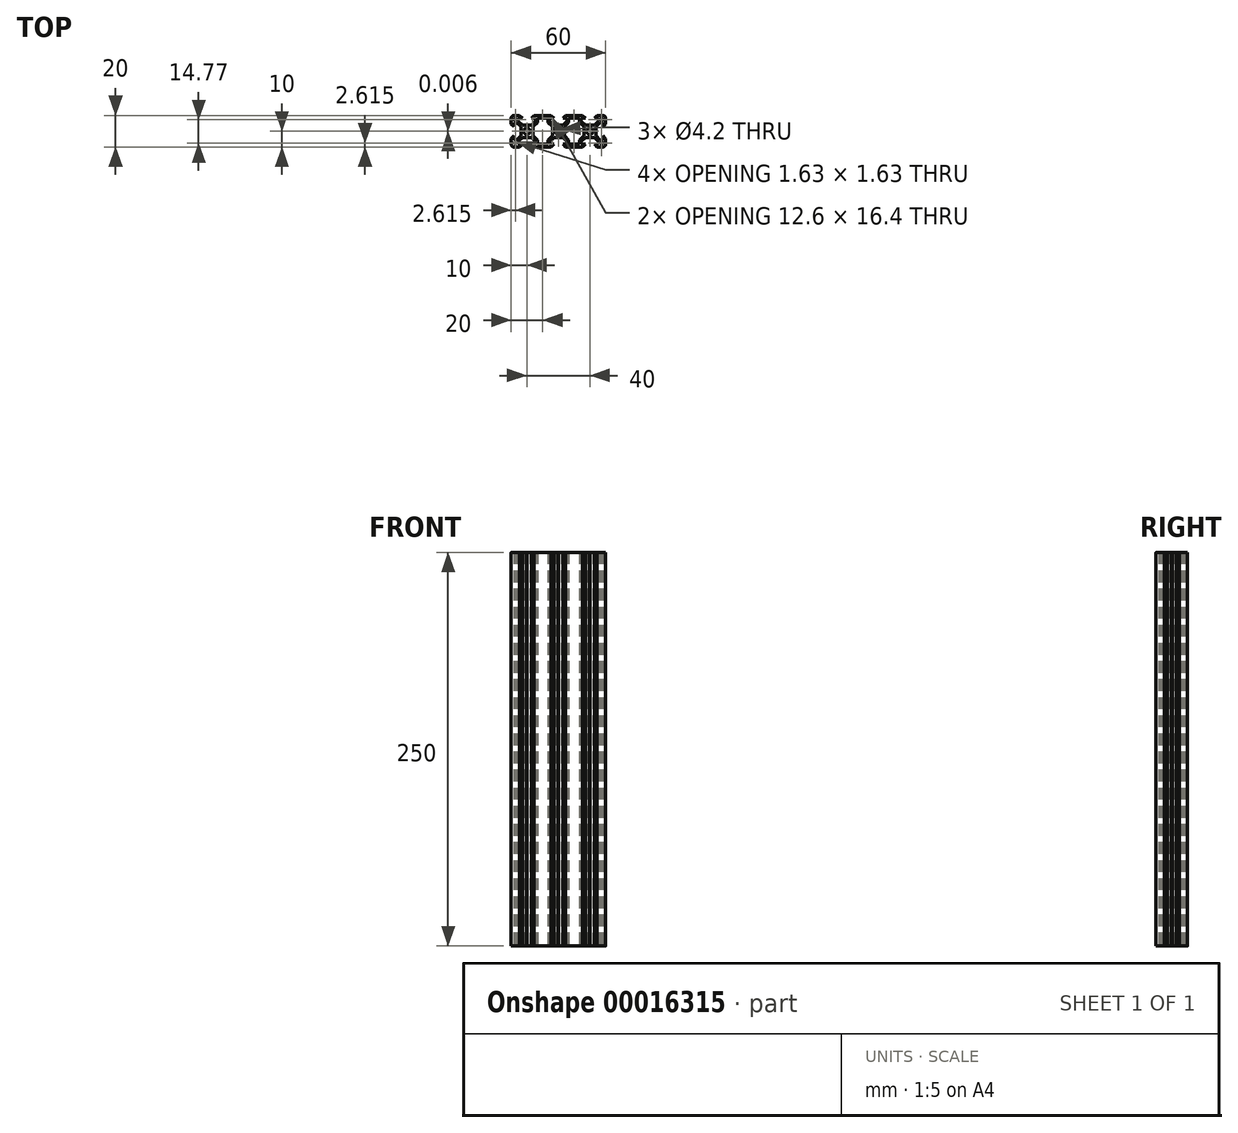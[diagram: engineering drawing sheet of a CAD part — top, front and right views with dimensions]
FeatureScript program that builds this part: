
annotation { "Feature Type Name" : "Feature", "Feature Type Description" : "" }
export const myFeature = defineFeature(function(context is Context, id is Id, definition is map)
    precondition{}
    {
        {
            var Q0;
            Q0=qCreatedBy(makeId("Top.planeOp"),FACE);
            var sketch = newSketch(context, id + "F0", { "sketchPlane" : qUnion([Q0])});
            skCircle(sketch, "E0", {"center": v(20, 0) * mm, "radius": 2.1 * mm});
            skLineSegment(sketch, "E1", {"start": v(-16.1, -2.84) * mm, "end": v(-13.43, -5.5) * mm});
            skLineSegment(sketch, "E2", {"start": v(-16.1, -0.2) * mm, "end": v(-16.1, -2.84) * mm});
            skLineSegment(sketch, "E3", {"start": v(-16.3, 0) * mm, "end": v(-16.1, -0.2) * mm});
            skLineSegment(sketch, "E4", {"start": v(-16.1, 0.2) * mm, "end": v(-16.3, 0) * mm});
            skLineSegment(sketch, "E5", {"start": v(-16.1, 2.84) * mm, "end": v(-16.1, 0.2) * mm});
            skLineSegment(sketch, "E6", {"start": v(-13.43, 5.5) * mm, "end": v(-16.1, 2.84) * mm});
            skLineSegment(sketch, "E7", {"start": v(-13.43, 8.2) * mm, "end": v(-13.43, 5.5) * mm});
            skLineSegment(sketch, "E8", {"start": v(-6.57, 8.2) * mm, "end": v(-13.43, 8.2) * mm});
            skLineSegment(sketch, "E9", {"start": v(-6.57, 5.5) * mm, "end": v(-6.57, 8.2) * mm});
            skLineSegment(sketch, "E10", {"start": v(-3.9, 2.84) * mm, "end": v(-6.57, 5.5) * mm});
            skLineSegment(sketch, "E11", {"start": v(-3.9, 0.2) * mm, "end": v(-3.9, 2.84) * mm});
            skLineSegment(sketch, "E12", {"start": v(-3.7, 0) * mm, "end": v(-3.9, 0.2) * mm});
            skLineSegment(sketch, "E13", {"start": v(-3.9, -0.2) * mm, "end": v(-3.7, 0) * mm});
            skLineSegment(sketch, "E14", {"start": v(-3.9, -2.84) * mm, "end": v(-3.9, -0.2) * mm});
            skLineSegment(sketch, "E15", {"start": v(-6.57, -5.5) * mm, "end": v(-3.9, -2.84) * mm});
            skLineSegment(sketch, "E16", {"start": v(-6.57, -8.2) * mm, "end": v(-6.57, -5.5) * mm});
            skLineSegment(sketch, "E17", {"start": v(-13.43, -8.2) * mm, "end": v(-6.57, -8.2) * mm});
            skLineSegment(sketch, "E18", {"start": v(-13.43, -5.5) * mm, "end": v(-13.43, -8.2) * mm});
            skLineSegment(sketch, "E19", {"start": v(26.57, 7.66) * mm, "end": v(27.66, 6.57) * mm});
            skLineSegment(sketch, "E20", {"start": v(26.57, 8.2) * mm, "end": v(26.57, 7.66) * mm});
            skLineSegment(sketch, "E21", {"start": v(28.2, 8.2) * mm, "end": v(26.57, 8.2) * mm});
            skLineSegment(sketch, "E22", {"start": v(28.2, 6.57) * mm, "end": v(28.2, 8.2) * mm});
            skLineSegment(sketch, "E23", {"start": v(27.66, 6.57) * mm, "end": v(28.2, 6.57) * mm});
            skLineSegment(sketch, "E24", {"start": v(27.66, -6.57) * mm, "end": v(26.57, -7.66) * mm});
            skLineSegment(sketch, "E25", {"start": v(28.2, -6.57) * mm, "end": v(27.66, -6.57) * mm});
            skLineSegment(sketch, "E26", {"start": v(28.2, -8.2) * mm, "end": v(28.2, -6.57) * mm});
            skLineSegment(sketch, "E27", {"start": v(26.57, -8.2) * mm, "end": v(28.2, -8.2) * mm});
            skLineSegment(sketch, "E28", {"start": v(26.57, -7.66) * mm, "end": v(26.57, -8.2) * mm});
            skLineSegment(sketch, "E29", {"start": v(-26.57, -7.66) * mm, "end": v(-27.66, -6.57) * mm});
            skLineSegment(sketch, "E30", {"start": v(-26.57, -8.2) * mm, "end": v(-26.57, -7.66) * mm});
            skLineSegment(sketch, "E31", {"start": v(-28.2, -8.2) * mm, "end": v(-26.57, -8.2) * mm});
            skLineSegment(sketch, "E32", {"start": v(-28.2, -6.57) * mm, "end": v(-28.2, -8.2) * mm});
            skLineSegment(sketch, "E33", {"start": v(-27.66, -6.57) * mm, "end": v(-28.2, -6.57) * mm});
            skLineSegment(sketch, "E34", {"start": v(-27.66, 6.57) * mm, "end": v(-26.57, 7.66) * mm});
            skLineSegment(sketch, "E35", {"start": v(-28.2, 6.57) * mm, "end": v(-27.66, 6.57) * mm});
            skLineSegment(sketch, "E36", {"start": v(-28.2, 8.2) * mm, "end": v(-28.2, 6.57) * mm});
            skLineSegment(sketch, "E37", {"start": v(-26.57, 8.2) * mm, "end": v(-28.2, 8.2) * mm});
            skLineSegment(sketch, "E38", {"start": v(-26.57, 7.66) * mm, "end": v(-26.57, 8.2) * mm});
            skLineSegment(sketch, "E39", {"start": v(-25.5, 8.2) * mm, "end": v(-22.84, 8.2) * mm});
            skLineSegment(sketch, "E40", {"start": v(-22.84, 8.2) * mm, "end": v(-24.64, 10) * mm});
            skLineSegment(sketch, "E41", {"start": v(-24.64, 10) * mm, "end": v(-28.2, 10) * mm});
            skArc(sketch, "E42", {"start": v(-28.2, 10) * mm, "mid": v(-29.47, 9.47) * mm, "end": v(-30, 8.2) * mm});
            skLineSegment(sketch, "E43", {"start": v(-30, 8.2) * mm, "end": v(-30, 4.64) * mm});
            skLineSegment(sketch, "E44", {"start": v(-30, 4.64) * mm, "end": v(-28.2, 2.84) * mm});
            skLineSegment(sketch, "E45", {"start": v(-28.2, 2.84) * mm, "end": v(-28.2, 5.5) * mm});
            skLineSegment(sketch, "E46", {"start": v(-28.2, 5.5) * mm, "end": v(-26.56, 5.5) * mm});
            skLineSegment(sketch, "E47", {"start": v(-26.56, 5.5) * mm, "end": v(-23.9, 2.84) * mm});
            skLineSegment(sketch, "E48", {"start": v(-23.9, 2.84) * mm, "end": v(-23.9, 0.2) * mm});
            skLineSegment(sketch, "E49", {"start": v(-23.9, 0.2) * mm, "end": v(-23.7, 0) * mm});
            skLineSegment(sketch, "E50", {"start": v(-23.7, 0) * mm, "end": v(-23.9, -0.2) * mm});
            skLineSegment(sketch, "E51", {"start": v(-23.9, -0.2) * mm, "end": v(-23.9, -2.84) * mm});
            skLineSegment(sketch, "E52", {"start": v(-23.9, -2.84) * mm, "end": v(-26.56, -5.5) * mm});
            skLineSegment(sketch, "E53", {"start": v(-26.56, -5.5) * mm, "end": v(-28.2, -5.5) * mm});
            skLineSegment(sketch, "E54", {"start": v(-28.2, -5.5) * mm, "end": v(-28.2, -2.84) * mm});
            skLineSegment(sketch, "E55", {"start": v(-28.2, -2.84) * mm, "end": v(-30, -4.64) * mm});
            skLineSegment(sketch, "E56", {"start": v(-30, -4.64) * mm, "end": v(-30, -8.2) * mm});
            skArc(sketch, "E57", {"start": v(-30, -8.2) * mm, "mid": v(-29.47, -9.47) * mm, "end": v(-28.2, -10) * mm});
            skLineSegment(sketch, "E58", {"start": v(-28.2, -10) * mm, "end": v(-24.64, -10) * mm});
            skLineSegment(sketch, "E59", {"start": v(-24.64, -10) * mm, "end": v(-22.84, -8.2) * mm});
            skLineSegment(sketch, "E60", {"start": v(-22.84, -8.2) * mm, "end": v(-25.5, -8.2) * mm});
            skLineSegment(sketch, "E61", {"start": v(-25.5, -8.2) * mm, "end": v(-25.5, -6.56) * mm});
            skLineSegment(sketch, "E62", {"start": v(-25.5, -6.56) * mm, "end": v(-22.84, -3.9) * mm});
            skLineSegment(sketch, "E63", {"start": v(-22.84, -3.9) * mm, "end": v(-20.2, -3.9) * mm});
            skLineSegment(sketch, "E64", {"start": v(-20.2, -3.9) * mm, "end": v(-20, -3.7) * mm});
            skLineSegment(sketch, "E65", {"start": v(-20, -3.7) * mm, "end": v(-19.8, -3.9) * mm});
            skLineSegment(sketch, "E66", {"start": v(-19.8, -3.9) * mm, "end": v(-17.16, -3.9) * mm});
            skLineSegment(sketch, "E67", {"start": v(-17.16, -3.9) * mm, "end": v(-14.5, -6.56) * mm});
            skLineSegment(sketch, "E68", {"start": v(-14.5, -6.56) * mm, "end": v(-14.5, -8.2) * mm});
            skLineSegment(sketch, "E69", {"start": v(-14.5, -8.2) * mm, "end": v(-17.16, -8.2) * mm});
            skLineSegment(sketch, "E70", {"start": v(-17.16, -8.2) * mm, "end": v(-15.36, -10) * mm});
            skLineSegment(sketch, "E71", {"start": v(-15.36, -10) * mm, "end": v(-4.64, -10) * mm});
            skLineSegment(sketch, "E72", {"start": v(-4.64, -10) * mm, "end": v(-2.84, -8.2) * mm});
            skLineSegment(sketch, "E73", {"start": v(-2.84, -8.2) * mm, "end": v(-5.5, -8.2) * mm});
            skLineSegment(sketch, "E74", {"start": v(-5.5, -8.2) * mm, "end": v(-5.5, -6.56) * mm});
            skLineSegment(sketch, "E75", {"start": v(-5.5, -6.56) * mm, "end": v(-2.84, -3.9) * mm});
            skLineSegment(sketch, "E76", {"start": v(-2.84, -3.9) * mm, "end": v(-0.2, -3.9) * mm});
            skLineSegment(sketch, "E77", {"start": v(-0.2, -3.9) * mm, "end": v(0, -3.7) * mm});
            skLineSegment(sketch, "E78", {"start": v(0, -3.7) * mm, "end": v(0.2, -3.9) * mm});
            skLineSegment(sketch, "E79", {"start": v(0.2, -3.9) * mm, "end": v(2.84, -3.9) * mm});
            skLineSegment(sketch, "E80", {"start": v(2.84, -3.9) * mm, "end": v(5.5, -6.56) * mm});
            skLineSegment(sketch, "E81", {"start": v(5.5, -6.56) * mm, "end": v(5.5, -8.2) * mm});
            skLineSegment(sketch, "E82", {"start": v(5.5, -8.2) * mm, "end": v(2.84, -8.2) * mm});
            skLineSegment(sketch, "E83", {"start": v(2.84, -8.2) * mm, "end": v(4.64, -10) * mm});
            skLineSegment(sketch, "E84", {"start": v(4.64, -10) * mm, "end": v(15.36, -10) * mm});
            skLineSegment(sketch, "E85", {"start": v(15.36, -10) * mm, "end": v(17.16, -8.2) * mm});
            skLineSegment(sketch, "E86", {"start": v(17.16, -8.2) * mm, "end": v(14.5, -8.2) * mm});
            skLineSegment(sketch, "E87", {"start": v(14.5, -8.2) * mm, "end": v(14.5, -6.56) * mm});
            skLineSegment(sketch, "E88", {"start": v(14.5, -6.56) * mm, "end": v(17.16, -3.9) * mm});
            skLineSegment(sketch, "E89", {"start": v(17.16, -3.9) * mm, "end": v(19.8, -3.9) * mm});
            skLineSegment(sketch, "E90", {"start": v(19.8, -3.9) * mm, "end": v(20, -3.7) * mm});
            skLineSegment(sketch, "E91", {"start": v(20, -3.7) * mm, "end": v(20.2, -3.9) * mm});
            skLineSegment(sketch, "E92", {"start": v(20.2, -3.9) * mm, "end": v(22.84, -3.9) * mm});
            skLineSegment(sketch, "E93", {"start": v(22.84, -3.9) * mm, "end": v(25.5, -6.56) * mm});
            skLineSegment(sketch, "E94", {"start": v(25.5, -6.56) * mm, "end": v(25.5, -8.2) * mm});
            skLineSegment(sketch, "E95", {"start": v(25.5, -8.2) * mm, "end": v(22.84, -8.2) * mm});
            skLineSegment(sketch, "E96", {"start": v(22.84, -8.2) * mm, "end": v(24.64, -10) * mm});
            skLineSegment(sketch, "E97", {"start": v(24.64, -10) * mm, "end": v(28.2, -10) * mm});
            skArc(sketch, "E98", {"start": v(28.2, -10) * mm, "mid": v(29.47, -9.47) * mm, "end": v(30, -8.2) * mm});
            skLineSegment(sketch, "E99", {"start": v(30, -8.2) * mm, "end": v(30, -4.64) * mm});
            skLineSegment(sketch, "E100", {"start": v(30, -4.64) * mm, "end": v(28.2, -2.84) * mm});
            skLineSegment(sketch, "E101", {"start": v(28.2, -2.84) * mm, "end": v(28.2, -5.5) * mm});
            skLineSegment(sketch, "E102", {"start": v(28.2, -5.5) * mm, "end": v(26.56, -5.5) * mm});
            skLineSegment(sketch, "E103", {"start": v(26.56, -5.5) * mm, "end": v(23.9, -2.84) * mm});
            skLineSegment(sketch, "E104", {"start": v(23.9, -2.84) * mm, "end": v(23.9, -0.2) * mm});
            skLineSegment(sketch, "E105", {"start": v(23.9, -0.2) * mm, "end": v(23.7, 0) * mm});
            skLineSegment(sketch, "E106", {"start": v(23.7, 0) * mm, "end": v(23.9, 0.2) * mm});
            skLineSegment(sketch, "E107", {"start": v(23.9, 0.2) * mm, "end": v(23.9, 2.84) * mm});
            skLineSegment(sketch, "E108", {"start": v(23.9, 2.84) * mm, "end": v(26.56, 5.5) * mm});
            skLineSegment(sketch, "E109", {"start": v(26.56, 5.5) * mm, "end": v(28.2, 5.5) * mm});
            skLineSegment(sketch, "E110", {"start": v(28.2, 5.5) * mm, "end": v(28.2, 2.84) * mm});
            skLineSegment(sketch, "E111", {"start": v(28.2, 2.84) * mm, "end": v(30, 4.64) * mm});
            skLineSegment(sketch, "E112", {"start": v(30, 4.64) * mm, "end": v(30, 8.2) * mm});
            skArc(sketch, "E113", {"start": v(30, 8.2) * mm, "mid": v(29.47, 9.47) * mm, "end": v(28.2, 10) * mm});
            skLineSegment(sketch, "E114", {"start": v(28.2, 10) * mm, "end": v(24.64, 10) * mm});
            skLineSegment(sketch, "E115", {"start": v(24.64, 10) * mm, "end": v(22.84, 8.2) * mm});
            skLineSegment(sketch, "E116", {"start": v(22.84, 8.2) * mm, "end": v(25.5, 8.2) * mm});
            skLineSegment(sketch, "E117", {"start": v(25.5, 8.2) * mm, "end": v(25.5, 6.56) * mm});
            skLineSegment(sketch, "E118", {"start": v(25.5, 6.56) * mm, "end": v(22.84, 3.9) * mm});
            skLineSegment(sketch, "E119", {"start": v(22.84, 3.9) * mm, "end": v(20.2, 3.9) * mm});
            skLineSegment(sketch, "E120", {"start": v(20.2, 3.9) * mm, "end": v(20, 3.7) * mm});
            skLineSegment(sketch, "E121", {"start": v(20, 3.7) * mm, "end": v(19.8, 3.9) * mm});
            skLineSegment(sketch, "E122", {"start": v(19.8, 3.9) * mm, "end": v(17.16, 3.9) * mm});
            skLineSegment(sketch, "E123", {"start": v(17.16, 3.9) * mm, "end": v(14.5, 6.56) * mm});
            skLineSegment(sketch, "E124", {"start": v(14.5, 6.56) * mm, "end": v(14.5, 8.2) * mm});
            skLineSegment(sketch, "E125", {"start": v(14.5, 8.2) * mm, "end": v(17.16, 8.2) * mm});
            skLineSegment(sketch, "E126", {"start": v(17.16, 8.2) * mm, "end": v(15.36, 10) * mm});
            skLineSegment(sketch, "E127", {"start": v(15.36, 10) * mm, "end": v(4.64, 10) * mm});
            skLineSegment(sketch, "E128", {"start": v(4.64, 10) * mm, "end": v(2.84, 8.2) * mm});
            skLineSegment(sketch, "E129", {"start": v(2.84, 8.2) * mm, "end": v(5.5, 8.2) * mm});
            skLineSegment(sketch, "E130", {"start": v(5.5, 8.2) * mm, "end": v(5.5, 6.56) * mm});
            skLineSegment(sketch, "E131", {"start": v(5.5, 6.56) * mm, "end": v(2.84, 3.9) * mm});
            skLineSegment(sketch, "E132", {"start": v(2.84, 3.9) * mm, "end": v(0.2, 3.9) * mm});
            skLineSegment(sketch, "E133", {"start": v(0.2, 3.9) * mm, "end": v(0, 3.7) * mm});
            skLineSegment(sketch, "E134", {"start": v(0, 3.7) * mm, "end": v(-0.2, 3.9) * mm});
            skLineSegment(sketch, "E135", {"start": v(-0.2, 3.9) * mm, "end": v(-2.84, 3.9) * mm});
            skLineSegment(sketch, "E136", {"start": v(-2.84, 3.9) * mm, "end": v(-5.5, 6.56) * mm});
            skLineSegment(sketch, "E137", {"start": v(-5.5, 6.56) * mm, "end": v(-5.5, 8.2) * mm});
            skLineSegment(sketch, "E138", {"start": v(-5.5, 8.2) * mm, "end": v(-2.84, 8.2) * mm});
            skLineSegment(sketch, "E139", {"start": v(-2.84, 8.2) * mm, "end": v(-4.64, 10) * mm});
            skLineSegment(sketch, "E140", {"start": v(-4.64, 10) * mm, "end": v(-15.36, 10) * mm});
            skLineSegment(sketch, "E141", {"start": v(-15.36, 10) * mm, "end": v(-17.16, 8.2) * mm});
            skLineSegment(sketch, "E142", {"start": v(-17.16, 8.2) * mm, "end": v(-14.5, 8.2) * mm});
            skLineSegment(sketch, "E143", {"start": v(-14.5, 8.2) * mm, "end": v(-14.5, 6.56) * mm});
            skLineSegment(sketch, "E144", {"start": v(-14.5, 6.56) * mm, "end": v(-17.16, 3.9) * mm});
            skLineSegment(sketch, "E145", {"start": v(-17.16, 3.9) * mm, "end": v(-19.8, 3.9) * mm});
            skLineSegment(sketch, "E146", {"start": v(-19.8, 3.9) * mm, "end": v(-20, 3.7) * mm});
            skLineSegment(sketch, "E147", {"start": v(-20, 3.7) * mm, "end": v(-20.2, 3.9) * mm});
            skLineSegment(sketch, "E148", {"start": v(-20.2, 3.9) * mm, "end": v(-22.84, 3.9) * mm});
            skLineSegment(sketch, "E149", {"start": v(-22.84, 3.9) * mm, "end": v(-25.5, 6.56) * mm});
            skLineSegment(sketch, "E150", {"start": v(-25.5, 6.56) * mm, "end": v(-25.5, 8.2) * mm});
            skCircle(sketch, "E151", {"center": v(-20, 0) * mm, "radius": 2.1 * mm});
            skLineSegment(sketch, "E152", {"start": v(16.1, 0.2) * mm, "end": v(16.1, 2.84) * mm});
            skLineSegment(sketch, "E153", {"start": v(16.3, 0) * mm, "end": v(16.1, 0.2) * mm});
            skLineSegment(sketch, "E154", {"start": v(16.1, -0.2) * mm, "end": v(16.3, 0) * mm});
            skLineSegment(sketch, "E155", {"start": v(16.1, -2.84) * mm, "end": v(16.1, -0.2) * mm});
            skLineSegment(sketch, "E156", {"start": v(13.43, -5.5) * mm, "end": v(16.1, -2.84) * mm});
            skLineSegment(sketch, "E157", {"start": v(13.43, -8.2) * mm, "end": v(13.43, -5.5) * mm});
            skLineSegment(sketch, "E158", {"start": v(6.57, -8.2) * mm, "end": v(13.43, -8.2) * mm});
            skLineSegment(sketch, "E159", {"start": v(6.57, -5.5) * mm, "end": v(6.57, -8.2) * mm});
            skLineSegment(sketch, "E160", {"start": v(3.9, -2.84) * mm, "end": v(6.57, -5.5) * mm});
            skLineSegment(sketch, "E161", {"start": v(3.9, -0.2) * mm, "end": v(3.9, -2.84) * mm});
            skLineSegment(sketch, "E162", {"start": v(3.7, 0) * mm, "end": v(3.9, -0.2) * mm});
            skLineSegment(sketch, "E163", {"start": v(3.9, 0.2) * mm, "end": v(3.7, 0) * mm});
            skLineSegment(sketch, "E164", {"start": v(3.9, 2.84) * mm, "end": v(3.9, 0.2) * mm});
            skLineSegment(sketch, "E165", {"start": v(6.57, 5.5) * mm, "end": v(3.9, 2.84) * mm});
            skLineSegment(sketch, "E166", {"start": v(6.57, 8.2) * mm, "end": v(6.57, 5.5) * mm});
            skLineSegment(sketch, "E167", {"start": v(13.43, 8.2) * mm, "end": v(6.57, 8.2) * mm});
            skLineSegment(sketch, "E168", {"start": v(13.43, 5.5) * mm, "end": v(13.43, 8.2) * mm});
            skLineSegment(sketch, "E169", {"start": v(16.1, 2.84) * mm, "end": v(13.43, 5.5) * mm});
            skCircle(sketch, "E170", {"center": v(0, 0) * mm, "radius": 2.1 * mm});
            skSolve(sketch);
        }
        {
            var Q0;
            Q0=qSketchRegion(id+"F0",true);
            extrude(context, id + "F1", {"entities" : qUnion([Q0]), "depth" : 250 * mm});
        }
    });
